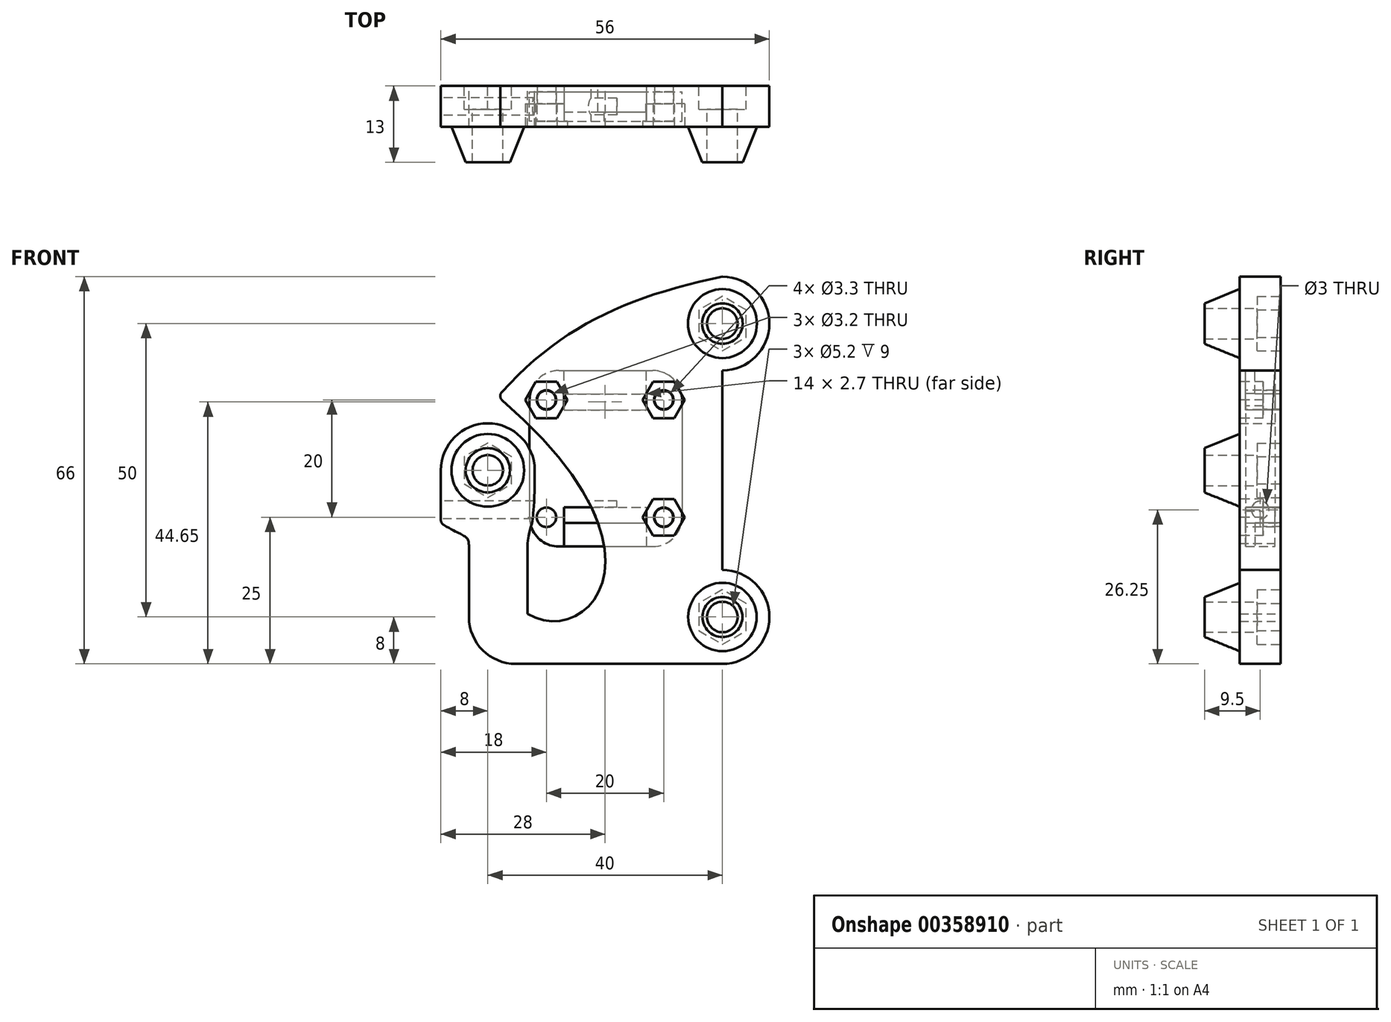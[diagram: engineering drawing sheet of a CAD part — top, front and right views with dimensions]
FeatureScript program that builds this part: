
annotation { "Feature Type Name" : "Feature", "Feature Type Description" : "" }
export const myFeature = defineFeature(function(context is Context, id is Id, definition is map)
    precondition{}
    {
        {
            var Q0;
            Q0=qCreatedBy(makeId("Front.planeOp"),FACE);
            var sketch = newSketch(context, id + "F0", { "sketchPlane" : qUnion([Q0])});
            skCircle(sketch, "E0", {"center": v(20, 25) * mm, "radius": 2.6 * mm});
            skCircle(sketch, "E1", {"center": v(20, -25) * mm, "radius": 2.6 * mm});
            skCircle(sketch, "E2", {"center": v(-20, 0) * mm, "radius": 2.6 * mm});
            skLineSegment(sketch, "E3", {"start": v(20, 25) * mm, "end": v(20, -25) * mm, "construction": true});
            skLineSegment(sketch, "E4", {"start": v(20, 17) * mm, "end": v(20, -17) * mm});
            skArc(sketch, "E5", {"start": v(20, 33) * mm, "mid": v(28, 25) * mm, "end": v(20, 17) * mm});
            skArc(sketch, "E6", {"start": v(20, -17) * mm, "mid": v(28, -25) * mm, "end": v(20, -33) * mm});
            skArc(sketch, "E7", {"start": v(-28, 0) * mm, "mid": v(-20, 8) * mm, "end": v(-12, 0) * mm});
            skLineSegment(sketch, "E8", {"start": v(20, -33) * mm, "end": v(-15.22, -33) * mm});
            skLineSegment(sketch, "E9", {"start": v(-23.22, -13) * mm, "end": v(-23.22, -25) * mm});
            skArc(sketch, "E10", {"start": v(-23.22, -25) * mm, "mid": v(-20.87, -30.66) * mm, "end": v(-15.22, -33) * mm});
            skLineSegment(sketch, "E11", {"start": v(-28, 0) * mm, "end": v(-28, -9) * mm});
            skFitSpline(sketch, "E12", {"points": [v(-28, -9) * mm, v(-23.22, -13) * mm], "startDerivative": vector(12.3, -7.77) * mm, "endDerivative": vector(0, -6.37) * mm});
            skLineSegment(sketch, "E13", {"start": v(-13.22, -12.44) * mm, "end": v(-13.22, -24.44) * mm});
            skFitSpline(sketch, "E14", {"points": [v(-12, 0) * mm, v(-13.22, -12.44) * mm], "startDerivative": vector(0, -32.3) * mm, "endDerivative": vector(-1.2, -11.64) * mm});
            skFitSpline(sketch, "E15", {"points": [v(20, 33) * mm, v(-18.3, 12.57) * mm], "startDerivative": vector(-48.68, -10.27) * mm, "endDerivative": vector(-32, -36.18) * mm});
            skFitSpline(sketch, "E16", {"points": [v(-18.3, 12.57) * mm, v(-13.22, -24.44) * mm], "startDerivative": vector(93.75, -79.12) * mm, "endDerivative": vector(-30.47, 18.44) * mm});
            skSolve(sketch);
        }
        {
            var Q0;
            Q0=qCreatedBy(makeId("Front.planeOp"),FACE);
            var sketch = newSketch(context, id + "F1", { "sketchPlane" : qUnion([Q0])});
            skLineSegment(sketch, "E17.bottom", {"start": v(-12.88, 17) * mm, "end": v(13.12, 17) * mm});
            skLineSegment(sketch, "E17.top", {"start": v(-12.88, -13) * mm, "end": v(13.12, -13) * mm});
            skLineSegment(sketch, "E17.left", {"start": v(-12.88, 17) * mm, "end": v(-12.88, -13) * mm});
            skLineSegment(sketch, "E17.right", {"start": v(13.12, 17) * mm, "end": v(13.12, -13) * mm});
            skPoint(sketch, "E17.middle", {"position": v(0.12, 2) * mm});
            skSolve(sketch);
        }
        {
            var Q0;
            Q0=makeQuery(id+"F0.imprint","IMPRINT",FACE,{"disambiguationData":[TD([[makeQuery(id+"F0.imprint","IMPRINT",EDGE,{"derivedFrom":sQuery(id+"F0.wireOp",EDGE,"E0")}),-1.0]])]});
            extrude(context, id + "F2", {"entities" : qUnion([Q0]), "endBound" : BoundingType.SYMMETRIC, "depth" : 7 * mm});
        }
        {
            var Q0;
            Q0=makeQuery(id+"F2.opExtrude","SWEPT_FACE",FACE,{"disambiguationData":[OSD([sQuery(id+"F0.wireOp",EDGE,"E11")])]});
            var sketch = newSketch(context, id + "F3", { "sketchPlane" : qUnion([Q0])});
            skCircle(sketch, "E18", {"center": v(0, -6.75) * mm, "radius": 1.5 * mm});
            skSolve(sketch);
        }
        {
            var Q0;
            Q0=makeQuery(id+"F3.imprint","IMPRINT",FACE,{"disambiguationData":[TD([[makeQuery(id+"F3.imprint","IMPRINT",EDGE,{"derivedFrom":sQuery(id+"F3.wireOp",EDGE,"E18")}),1.0]])]});
            extrude(context, id + "F4", {"entities" : qUnion([Q0]), "operationType" : NewBodyOperationType.REMOVE, "oppositeDirection" : true, "depth" : 30 * mm});
        }
        {
            var Q0;
            Q0=makeQuery(id+"F2.opExtrude","SWEPT_EDGE",EDGE,{"disambiguationData":[OSD([sQuery(id+"F0.wireOp",EDGE,"E11"),sQuery(id+"F0.wireOp",EDGE,"E12")])]});
            var Q1;
            Q1=makeQuery(id+"F2.opExtrude","SWEPT_EDGE",EDGE,{"disambiguationData":[OSD([sQuery(id+"F0.wireOp",EDGE,"y4eGnbCm-3Hrs-5hrD-dIgi-gNOgpB39MgVZ"),sQuery(id+"F0.wireOp",EDGE,"ed54e055-604d-4025-95d1-e6f78dbeb488")])]});
            var Q2;
            Q2=makeQuery(id+"F2.opExtrude","SWEPT_EDGE",EDGE,{"disambiguationData":[OSD([sQuery(id+"F0.wireOp",EDGE,"E15"),sQuery(id+"F0.wireOp",EDGE,"E16")])]});
            fillet(context, id + "F5", {"entities" : qUnion([Q0, Q1, Q2]), "radius" : 1 * mm, "tangentPropagation" : true, "allowEdgeOverflow" : false});
        }
        {
            var Q0;
            Q0=makeQuery(id+"F2.opExtrude","CAP_FACE",FACE,{"disambiguationData":[OSD([sQuery(id+"F0.wireOp",EDGE,"E0"),sQuery(id+"F0.wireOp",EDGE,"E1"),sQuery(id+"F0.wireOp",EDGE,"E2"),sQuery(id+"F0.wireOp",EDGE,"y4eGnbCm-3Hrs-5hrD-dIgi-gNOgpB39MgVZ"),sQuery(id+"F0.wireOp",EDGE,"E4"),sQuery(id+"F0.wireOp",EDGE,"BUwMD9Xc-JiU5-OSMk-13Fp-rfpNMY0ihcZR"),sQuery(id+"F0.wireOp",EDGE,"E5"),sQuery(id+"F0.wireOp",EDGE,"12f08c4f-c35a-4e5f-80f0-837b022aba71"),sQuery(id+"F0.wireOp",EDGE,"E6"),sQuery(id+"F0.wireOp",EDGE,"E7"),sQuery(id+"F0.wireOp",EDGE,"E8"),sQuery(id+"F0.wireOp",EDGE,"E9"),sQuery(id+"F0.wireOp",EDGE,"E10"),sQuery(id+"F0.wireOp",EDGE,"E11"),sQuery(id+"F0.wireOp",EDGE,"E12"),sQuery(id+"F0.wireOp",EDGE,"E13"),sQuery(id+"F0.wireOp",EDGE,"E14"),sQuery(id+"F0.wireOp",EDGE,"7afQjAC8-U2vp-nMDg-Dxe4-XbSwWssdFdVV"),sQuery(id+"F0.wireOp",EDGE,"192d52ab-e9b2-4977-b37f-87d5d9081c97"),sQuery(id+"F0.wireOp",EDGE,"ed54e055-604d-4025-95d1-e6f78dbeb488")])],"isStart":true});
            var sketch = newSketch(context, id + "F6", { "sketchPlane" : qUnion([Q0])});
            skCircle(sketch, "E19.cCircle", {"center": v(-20, 25) * mm, "radius": 4.65 * mm, "construction": true});
            skLineSegment(sketch, "E19.0", {"start": v(-20, 20.35) * mm, "end": v(-24.03, 22.67) * mm});
            skLineSegment(sketch, "E19.1", {"start": v(-24.03, 22.67) * mm, "end": v(-24.03, 27.33) * mm});
            skLineSegment(sketch, "E19.2", {"start": v(-24.03, 27.33) * mm, "end": v(-20, 29.65) * mm});
            skLineSegment(sketch, "E19.3", {"start": v(-20, 29.65) * mm, "end": v(-15.97, 27.33) * mm});
            skLineSegment(sketch, "E19.4", {"start": v(-15.97, 27.33) * mm, "end": v(-15.97, 22.68) * mm});
            skLineSegment(sketch, "E19.5", {"start": v(-15.97, 22.68) * mm, "end": v(-20, 20.35) * mm});
            skCircle(sketch, "E20.cCircle", {"center": v(20, 0) * mm, "radius": 4.65 * mm, "construction": true});
            skLineSegment(sketch, "E20.0", {"start": v(20, -4.65) * mm, "end": v(15.97, -2.33) * mm});
            skLineSegment(sketch, "E20.1", {"start": v(15.97, -2.32) * mm, "end": v(15.97, 2.33) * mm});
            skLineSegment(sketch, "E20.2", {"start": v(15.97, 2.33) * mm, "end": v(20, 4.65) * mm});
            skLineSegment(sketch, "E20.3", {"start": v(20, 4.65) * mm, "end": v(24.03, 2.33) * mm});
            skLineSegment(sketch, "E20.4", {"start": v(24.03, 2.33) * mm, "end": v(24.03, -2.33) * mm});
            skLineSegment(sketch, "E20.5", {"start": v(24.03, -2.33) * mm, "end": v(20, -4.65) * mm});
            skCircle(sketch, "E21.cCircle", {"center": v(-20, -25) * mm, "radius": 4.65 * mm, "construction": true});
            skLineSegment(sketch, "E21.0", {"start": v(-20, -29.65) * mm, "end": v(-24.03, -27.33) * mm});
            skLineSegment(sketch, "E21.1", {"start": v(-24.03, -27.33) * mm, "end": v(-24.03, -22.68) * mm});
            skLineSegment(sketch, "E21.2", {"start": v(-24.03, -22.68) * mm, "end": v(-20, -20.35) * mm});
            skLineSegment(sketch, "E21.3", {"start": v(-20, -20.35) * mm, "end": v(-15.97, -22.67) * mm});
            skLineSegment(sketch, "E21.4", {"start": v(-15.97, -22.67) * mm, "end": v(-15.97, -27.32) * mm});
            skLineSegment(sketch, "E21.5", {"start": v(-15.97, -27.32) * mm, "end": v(-20, -29.65) * mm});
            skSolve(sketch);
        }
        {
            var Q0;
            Q0=makeQuery(id+"F6.imprint","IMPRINT",FACE,{"disambiguationData":[TD([[makeQuery(id+"F6.imprint","IMPRINT",EDGE,{"derivedFrom":sQuery(id+"F6.wireOp",EDGE,"E21.0")}),-1.0]])]});
            var Q1;
            Q1=makeQuery(id+"F6.imprint","IMPRINT",FACE,{"disambiguationData":[TD([[makeQuery(id+"F6.imprint","IMPRINT",EDGE,{"derivedFrom":sQuery(id+"F6.wireOp",EDGE,"E20.0")}),-1.0]])]});
            var Q2;
            Q2=makeQuery(id+"F6.imprint","IMPRINT",FACE,{"disambiguationData":[TD([[makeQuery(id+"F6.imprint","IMPRINT",EDGE,{"derivedFrom":sQuery(id+"F6.wireOp",EDGE,"E19.0")}),-1.0]])]});
            extrude(context, id + "F7", {"entities" : qUnion([Q0, Q1, Q2]), "operationType" : NewBodyOperationType.REMOVE, "oppositeDirection" : true, "depth" : 4 * mm});
        }
        {
            var Q0;
            Q0=makeQuery(id+"F2.opExtrude","CAP_FACE",FACE,{"disambiguationData":[OSD([sQuery(id+"F0.wireOp",EDGE,"E0"),sQuery(id+"F0.wireOp",EDGE,"E1"),sQuery(id+"F0.wireOp",EDGE,"E2"),sQuery(id+"F0.wireOp",EDGE,"y4eGnbCm-3Hrs-5hrD-dIgi-gNOgpB39MgVZ"),sQuery(id+"F0.wireOp",EDGE,"E4"),sQuery(id+"F0.wireOp",EDGE,"BUwMD9Xc-JiU5-OSMk-13Fp-rfpNMY0ihcZR"),sQuery(id+"F0.wireOp",EDGE,"E5"),sQuery(id+"F0.wireOp",EDGE,"12f08c4f-c35a-4e5f-80f0-837b022aba71"),sQuery(id+"F0.wireOp",EDGE,"E6"),sQuery(id+"F0.wireOp",EDGE,"E7"),sQuery(id+"F0.wireOp",EDGE,"E8"),sQuery(id+"F0.wireOp",EDGE,"E9"),sQuery(id+"F0.wireOp",EDGE,"E10"),sQuery(id+"F0.wireOp",EDGE,"E11"),sQuery(id+"F0.wireOp",EDGE,"E12"),sQuery(id+"F0.wireOp",EDGE,"E13"),sQuery(id+"F0.wireOp",EDGE,"E14"),sQuery(id+"F0.wireOp",EDGE,"7afQjAC8-U2vp-nMDg-Dxe4-XbSwWssdFdVV"),sQuery(id+"F0.wireOp",EDGE,"192d52ab-e9b2-4977-b37f-87d5d9081c97"),sQuery(id+"F0.wireOp",EDGE,"ed54e055-604d-4025-95d1-e6f78dbeb488")])],"isStart":false});
            var sketch = newSketch(context, id + "F8", { "sketchPlane" : qUnion([Q0])});
            skCircle(sketch, "E22", {"center": v(10, 12) * mm, "radius": 1.6 * mm});
            skCircle(sketch, "E23.1.0.0", {"center": v(-10, 12) * mm, "radius": 1.6 * mm});
            skLineSegment(sketch, "E23.direction1", {"start": v(10, 12) * mm, "end": v(-10, 12) * mm, "construction": true});
            skLineSegment(sketch, "E23.direction2", {"start": v(10, 12) * mm, "end": v(10, -8) * mm, "construction": true});
            skCircle(sketch, "E24.0.0.1", {"center": v(10, -8) * mm, "radius": 1.6 * mm});
            skCircle(sketch, "E25.0.0.1", {"center": v(-10, -8) * mm, "radius": 1.6 * mm});
            skSolve(sketch);
        }
        {
            var Q0;
            Q0 = qSketchRegion(id + "F8", true);
            extrude(context, id + "F9", {"entities" : qUnion([Q0]), "operationType" : NewBodyOperationType.REMOVE, "endBound" : BoundingType.THROUGH_ALL, "oppositeDirection" : true, "depth" : 25 * mm});
        }
        {
            var Q0;
            {var subQ0=sQuery(id+"F0.wireOp",EDGE,"ed54e055-604d-4025-95d1-e6f78dbeb488");var subQ1=sQuery(id+"F0.wireOp",EDGE,"y4eGnbCm-3Hrs-5hrD-dIgi-gNOgpB39MgVZ");var subQ2=sQuery(id+"F0.wireOp",EDGE,"192d52ab-e9b2-4977-b37f-87d5d9081c97");var subQ3=sQuery(id+"F0.wireOp",EDGE,"7afQjAC8-U2vp-nMDg-Dxe4-XbSwWssdFdVV");var subQ4=sQuery(id+"F0.wireOp",EDGE,"E14");var subQ5=sQuery(id+"F0.wireOp",EDGE,"E13");var subQ6=sQuery(id+"F0.wireOp",EDGE,"E12");var subQ7=sQuery(id+"F0.wireOp",EDGE,"E11");var subQ8=sQuery(id+"F0.wireOp",EDGE,"E10");var subQ9=sQuery(id+"F0.wireOp",EDGE,"E9");var subQ10=sQuery(id+"F0.wireOp",EDGE,"E8");var subQ11=sQuery(id+"F0.wireOp",EDGE,"E2");var subQ12=sQuery(id+"F0.wireOp",EDGE,"E1");var subQ13=sQuery(id+"F0.wireOp",EDGE,"E0");var subQ14=sQuery(id+"F0.wireOp",EDGE,"E7");var subQ15=sQuery(id+"F0.wireOp",EDGE,"E4");var subQ16=sQuery(id+"F0.wireOp",EDGE,"BUwMD9Xc-JiU5-OSMk-13Fp-rfpNMY0ihcZR");var subQ17=sQuery(id+"F0.wireOp",EDGE,"E5");var subQ18=sQuery(id+"F0.wireOp",EDGE,"12f08c4f-c35a-4e5f-80f0-837b022aba71");var subQ19=sQuery(id+"F0.wireOp",EDGE,"E6");Q0=makeQuery(id+"F9.boolean.opBoolean","SPLIT",FACE,{"disambiguationData":[TD([makeQuery(id+"F2.opExtrude","SWEPT_FACE",FACE,{"disambiguationData":[OSD([subQ13])]})])],"derivedFrom":makeQuery(id+"F2.opExtrude","CAP_FACE",FACE,{"disambiguationData":[OSD([subQ13,subQ12,subQ11,subQ1,subQ15,subQ16,subQ17,subQ18,subQ19,subQ14,subQ10,subQ9,subQ8,subQ7,subQ6,subQ5,subQ4,subQ3,subQ2,subQ0])],"isStart":false})});}
            var sketch = newSketch(context, id + "F10", { "sketchPlane" : qUnion([Q0])});
            skCircle(sketch, "E26.cCircle", {"center": v(-10, 12) * mm, "radius": 3.6 * mm, "construction": true});
            skLineSegment(sketch, "E26.0", {"start": v(-6.4, 12) * mm, "end": v(-8.2, 8.88) * mm});
            skLineSegment(sketch, "E26.1", {"start": v(-8.2, 8.88) * mm, "end": v(-11.8, 8.88) * mm});
            skLineSegment(sketch, "E26.2", {"start": v(-11.8, 8.88) * mm, "end": v(-13.6, 12) * mm});
            skLineSegment(sketch, "E26.3", {"start": v(-13.6, 12) * mm, "end": v(-11.8, 15.12) * mm});
            skLineSegment(sketch, "E26.4", {"start": v(-11.8, 15.12) * mm, "end": v(-8.2, 15.12) * mm});
            skLineSegment(sketch, "E26.5", {"start": v(-8.2, 15.12) * mm, "end": v(-6.4, 12) * mm});
            skLineSegment(sketch, "E27.1.0.0", {"start": v(11.8, 15.12) * mm, "end": v(13.6, 12) * mm});
            skLineSegment(sketch, "E27.1.0.1", {"start": v(8.2, 15.12) * mm, "end": v(11.8, 15.12) * mm});
            skLineSegment(sketch, "E27.1.0.2", {"start": v(6.4, 12) * mm, "end": v(8.2, 15.12) * mm});
            skLineSegment(sketch, "E27.1.0.3", {"start": v(8.2, 8.88) * mm, "end": v(6.4, 12) * mm});
            skLineSegment(sketch, "E27.1.0.4", {"start": v(11.8, 8.88) * mm, "end": v(8.2, 8.88) * mm});
            skLineSegment(sketch, "E27.1.0.5", {"start": v(13.6, 12) * mm, "end": v(11.8, 8.88) * mm});
            skCircle(sketch, "E27.1.0.6", {"center": v(10, 12) * mm, "radius": 3.6 * mm, "construction": true});
            skLineSegment(sketch, "E27.1.1.0", {"start": v(11.8, -4.88) * mm, "end": v(13.6, -8) * mm});
            skLineSegment(sketch, "E27.1.1.1", {"start": v(8.2, -4.88) * mm, "end": v(11.8, -4.88) * mm});
            skLineSegment(sketch, "E27.1.1.2", {"start": v(6.4, -8) * mm, "end": v(8.2, -4.88) * mm});
            skLineSegment(sketch, "E27.1.1.3", {"start": v(8.2, -11.12) * mm, "end": v(6.4, -8) * mm});
            skLineSegment(sketch, "E27.1.1.4", {"start": v(11.8, -11.12) * mm, "end": v(8.2, -11.12) * mm});
            skLineSegment(sketch, "E27.1.1.5", {"start": v(13.6, -8) * mm, "end": v(11.8, -11.12) * mm});
            skCircle(sketch, "E27.1.1.6", {"center": v(10, -8) * mm, "radius": 3.6 * mm, "construction": true});
            skLineSegment(sketch, "E27.direction1", {"start": v(-11.8, 8.88) * mm, "end": v(8.2, 8.88) * mm, "construction": true});
            skLineSegment(sketch, "E27.direction2", {"start": v(-11.8, 8.88) * mm, "end": v(-11.8, -11.12) * mm, "construction": true});
            skSolve(sketch);
        }
        {
            var Q0;
            Q0 = qSketchRegion(id + "F10", true);
            extrude(context, id + "F11", {"entities" : qUnion([Q0]), "operationType" : NewBodyOperationType.REMOVE, "oppositeDirection" : true, "depth" : 4 * mm});
        }
        {
            var Q0;
            Q0=makeQuery(id+"F8.imprint","IMPRINT",FACE,{"disambiguationData":[TD([[makeQuery(id+"F8.imprint","IMPRINT",EDGE,{"derivedFrom":sQuery(id+"F8.wireOp",EDGE,"E22")}),-1.0]])]});
            cPlane(context, id + "F12", {"entities" : qUnion([Q0]), "cplaneType" : CPlaneType.OFFSET, "offset" : 0 * mm, "width" : 150 * mm, "height" : 150 * mm});
        }
        {
            var Q0;
            Q0=qCreatedBy(id+"F12.planeOp",FACE);
            var sketch = newSketch(context, id + "F13", { "sketchPlane" : qUnion([Q0])});
            skCircle(sketch, "E28", {"center": v(-20, 0) * mm, "radius": 6.2 * mm});
            skCircle(sketch, "E29", {"center": v(20, 25) * mm, "radius": 5.88 * mm});
            skCircle(sketch, "E30", {"center": v(20, -25) * mm, "radius": 5.83 * mm});
            skSolve(sketch);
        }
        {
            var Q0;
            Q0 = qSketchRegion(id + "F13", true);
            extrude(context, id + "F14", {"entities" : qUnion([Q0]), "operationType" : NewBodyOperationType.ADD, "depth" : 6 * mm, "hasDraft" : true, "draftAngle" : 22 * degree, "draftPullDirection" : true});
        }
        {
            var Q0;
            Q0=makeQuery(id+"F0.imprint","IMPRINT",FACE,{"disambiguationData":[TD([[makeQuery(id+"F0.imprint","IMPRINT",EDGE,{"derivedFrom":sQuery(id+"F0.wireOp",EDGE,"E1")}),1.0]])]});
            var Q1;
            Q1=makeQuery(id+"F0.imprint","IMPRINT",FACE,{"disambiguationData":[TD([[makeQuery(id+"F0.imprint","IMPRINT",EDGE,{"derivedFrom":sQuery(id+"F0.wireOp",EDGE,"E0")}),1.0]])]});
            var Q2;
            Q2=makeQuery(id+"F0.imprint","IMPRINT",FACE,{"disambiguationData":[TD([[makeQuery(id+"F0.imprint","IMPRINT",EDGE,{"derivedFrom":sQuery(id+"F0.wireOp",EDGE,"E2")}),1.0]])]});
            extrude(context, id + "F15", {"entities" : qUnion([Q0, Q1, Q2]), "operationType" : NewBodyOperationType.REMOVE, "endBound" : BoundingType.THROUGH_ALL, "depth" : 25 * mm});
        }
        {
            var Q0;
            Q0 = qSketchRegion(id + "F1", true);
            extrude(context, id + "F16", {"entities" : qUnion([Q0]), "endBound" : BoundingType.SYMMETRIC, "depth" : 5 * mm});
        }
        {
            var Q0;
            Q0=makeQuery(id+"F16.opExtrude","SWEPT_EDGE",EDGE,{"disambiguationData":[OSD([sQuery(id+"F1.wireOp",EDGE,"E17.bottom"),sQuery(id+"F1.wireOp",EDGE,"E17.left")])]});
            var Q1;
            Q1=makeQuery(id+"F16.opExtrude","SWEPT_EDGE",EDGE,{"disambiguationData":[OSD([sQuery(id+"F1.wireOp",EDGE,"E17.top"),sQuery(id+"F1.wireOp",EDGE,"E17.left")])]});
            var Q2;
            Q2=makeQuery(id+"F16.opExtrude","SWEPT_EDGE",EDGE,{"disambiguationData":[OSD([sQuery(id+"F1.wireOp",EDGE,"E17.bottom"),sQuery(id+"F1.wireOp",EDGE,"E17.right")])]});
            var Q3;
            Q3=makeQuery(id+"F16.opExtrude","SWEPT_EDGE",EDGE,{"disambiguationData":[OSD([sQuery(id+"F1.wireOp",EDGE,"E17.top"),sQuery(id+"F1.wireOp",EDGE,"E17.right")])]});
            fillet(context, id + "F17", {"entities" : qUnion([Q0, Q1, Q2, Q3]), "radius" : 5 * mm, "tangentPropagation" : true, "allowEdgeOverflow" : false});
        }
        {
            var Q0;
            Q0=sQuery(id+"F8.wireOp",VERTEX,"E23.direction1.start");
            var Q1;
            Q1=sQuery(id+"F8.wireOp",VERTEX,"E23.1.0.0.center");
            var Q2;
            Q2=sQuery(id+"F8.wireOp",VERTEX,"E25.0.0.1.center");
            var Q3;
            Q3=sQuery(id+"F8.wireOp",VERTEX,"E24.0.0.1.center");
            var Q4;
            Q4=makeQuery(id+"F16.opExtrude","SWEPT_BODY",BODY,{"disambiguationData":[OSD([sQuery(id+"F1.wireOp",EDGE,"E17.bottom"),sQuery(id+"F1.wireOp",EDGE,"E17.top"),sQuery(id+"F1.wireOp",EDGE,"E17.left"),sQuery(id+"F1.wireOp",EDGE,"E17.right")])]});
            hole(context, id + "F18", {"style" : HoleStyle.SIMPLE, "endStyle" : HoleEndStyle.THROUGH, "standardTappedOrClearance" : lookupTablePath({ "standard" : "ISO", "fit" : "Normal", "size" : "M3", "type" : "Clearance" }), "standardBlindInLast" : lookupTablePath({ "fit" : "Standard", "standard" : "ISO", "size" : "M3", "type" : "Clearance" }), "holeDiameter" : 3.3 * mm, "isTappedThrough" : true, "tappedDepth" : 12 * mm, "tapClearance" : 3, "startFromSketch" : true, "locations" : qUnion([Q0, Q1, Q2, Q3]), "scope" : qUnion([Q4])});
        }
        {
            var Q0;
            Q0=makeQuery(id+"F16.opExtrude","CAP_FACE",FACE,{"disambiguationData":[OSD([sQuery(id+"F1.wireOp",EDGE,"E17.bottom"),sQuery(id+"F1.wireOp",EDGE,"E17.top"),sQuery(id+"F1.wireOp",EDGE,"E17.left"),sQuery(id+"F1.wireOp",EDGE,"E17.right")])],"isStart":false});
            var sketch = newSketch(context, id + "F19", { "sketchPlane" : qUnion([Q0])});
            skLineSegment(sketch, "E31.bottom", {"start": v(-7, -9) * mm, "end": v(7, -9) * mm});
            skLineSegment(sketch, "E31.top", {"start": v(-7, -13) * mm, "end": v(7, -13) * mm});
            skLineSegment(sketch, "E31.left", {"start": v(-7, -9) * mm, "end": v(-7, -13) * mm});
            skLineSegment(sketch, "E31.right", {"start": v(7, -9) * mm, "end": v(7, -13) * mm});
            skPoint(sketch, "E31.middle", {"position": v(0, -11) * mm});
            skLineSegment(sketch, "E32", {"start": v(-7, -9) * mm, "end": v(-7, -6.3) * mm});
            skLineSegment(sketch, "E33", {"start": v(-7, -6.3) * mm, "end": v(7, -6.3) * mm});
            skLineSegment(sketch, "E34", {"start": v(7, -6.3) * mm, "end": v(7, -9) * mm});
            skLineSegment(sketch, "E35", {"start": v(0, 2) * mm, "end": v(-12.88, 2) * mm, "construction": true});
            skLineSegment(sketch, "E36", {"start": v(-12.88, 2) * mm, "end": v(13.12, 2) * mm, "construction": true});
            skLineSegment(sketch, "E37.MirrorCS", {"start": v(7, 10.3) * mm, "end": v(7, 13) * mm});
            skLineSegment(sketch, "E38.MirrorCS", {"start": v(-7, 13) * mm, "end": v(-7, 17) * mm});
            skLineSegment(sketch, "E39.MirrorCS", {"start": v(-7, 10.3) * mm, "end": v(7, 10.3) * mm});
            skLineSegment(sketch, "E40.MirrorCS", {"start": v(-7, 13) * mm, "end": v(7, 13) * mm});
            skPoint(sketch, "E41.MirrorP", {"position": v(0, 15) * mm});
            skLineSegment(sketch, "E42.MirrorCS", {"start": v(7, 13) * mm, "end": v(7, 17) * mm});
            skLineSegment(sketch, "E43.MirrorCS", {"start": v(-7, 13) * mm, "end": v(-7, 10.3) * mm});
            skLineSegment(sketch, "E44.MirrorCS", {"start": v(-7, 17) * mm, "end": v(7, 17) * mm});
            skSolve(sketch);
        }
        {
            var Q0;
            Q0=makeQuery(id+"F19.imprint","IMPRINT",FACE,{"disambiguationData":[TD([[makeQuery(id+"F19.imprint","IMPRINT",EDGE,{"derivedFrom":sQuery(id+"F19.wireOp",EDGE,"E38.MirrorCS")}),-1.0]])]});
            var Q1;
            Q1=makeQuery(id+"F19.imprint","IMPRINT",FACE,{"disambiguationData":[TD([[makeQuery(id+"F19.imprint","IMPRINT",EDGE,{"derivedFrom":sQuery(id+"F19.wireOp",EDGE,"E31.bottom")}),-1.0]])]});
            extrude(context, id + "F20", {"entities" : qUnion([Q0, Q1]), "operationType" : NewBodyOperationType.REMOVE, "oppositeDirection" : true, "depth" : 1.6 * mm});
        }
        {
            var Q0;
            Q0=makeQuery(id+"F19.imprint","IMPRINT",FACE,{"disambiguationData":[TD([[makeQuery(id+"F19.imprint","IMPRINT",EDGE,{"derivedFrom":sQuery(id+"F19.wireOp",EDGE,"E31.bottom")}),1.0]])]});
            var Q1;
            Q1=makeQuery(id+"F19.imprint","IMPRINT",FACE,{"disambiguationData":[TD([[makeQuery(id+"F19.imprint","IMPRINT",EDGE,{"derivedFrom":sQuery(id+"F19.wireOp",EDGE,"E37.MirrorCS")}),1.0]])]});
            extrude(context, id + "F21", {"entities" : qUnion([Q0, Q1]), "operationType" : NewBodyOperationType.REMOVE, "endBound" : BoundingType.THROUGH_ALL, "oppositeDirection" : true, "depth" : 25 * mm});
        }
    });
